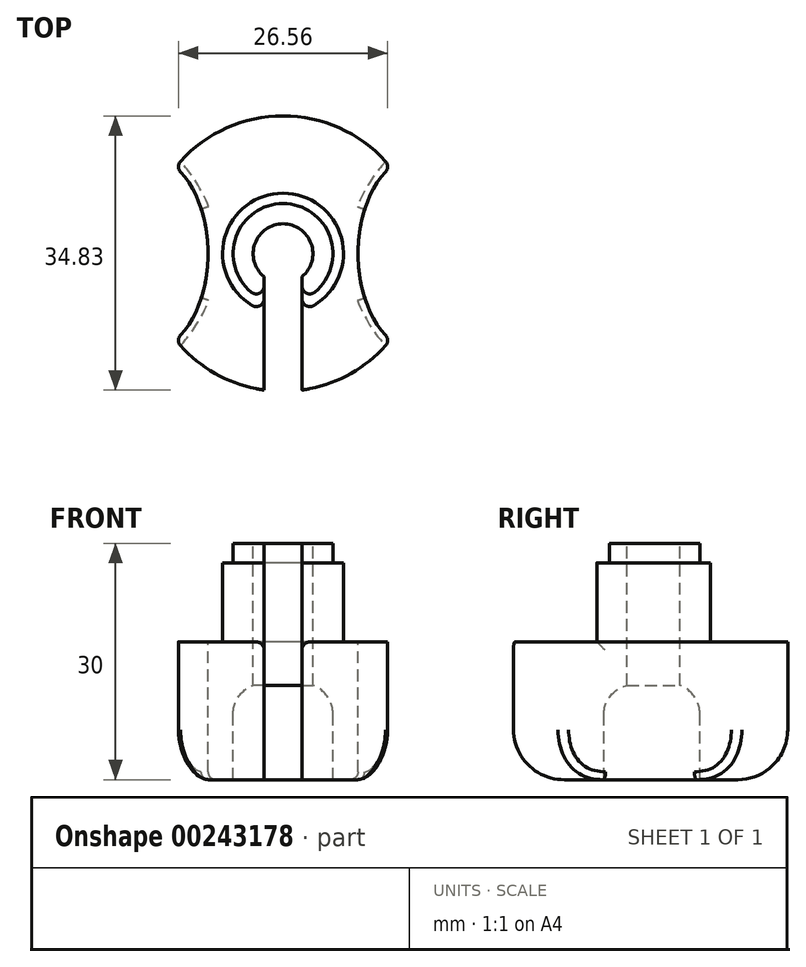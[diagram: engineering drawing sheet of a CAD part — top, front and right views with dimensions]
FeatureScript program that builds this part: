
annotation { "Feature Type Name" : "Feature", "Feature Type Description" : "" }
export const myFeature = defineFeature(function(context is Context, id is Id, definition is map)
    precondition{}
    {
        {
            var Q0;
            Q0=qCreatedBy(makeId("Top.planeOp"),FACE);
            var sketch = newSketch(context, id + "F0", { "sketchPlane" : qUnion([Q0])});
            skCircle(sketch, "E0", {"center": v(0, 0) * mm, "radius": 3.8 * mm});
            skCircle(sketch, "E1", {"center": v(0, 0) * mm, "radius": 6.35 * mm});
            skCircle(sketch, "E2", {"center": v(0, 0) * mm, "radius": 7.68 * mm});
            skCircle(sketch, "E3", {"center": v(0, 0) * mm, "radius": 17.5 * mm});
            skLineSegment(sketch, "E4", {"start": v(0, -2.92) * mm, "end": v(-2.41, -2.92) * mm});
            skLineSegment(sketch, "E5", {"start": v(0, -2.92) * mm, "end": v(2.41, -2.92) * mm});
            skLineSegment(sketch, "E6", {"start": v(-2.41, -2.92) * mm, "end": v(-2.41, -17.33) * mm});
            skLineSegment(sketch, "E7", {"start": v(2.41, -2.92) * mm, "end": v(2.41, -17.33) * mm});
            skLineSegment(sketch, "E8", {"start": v(0, 0) * mm, "end": v(-9.53, 0) * mm});
            skLineSegment(sketch, "E9", {"start": v(0, 0) * mm, "end": v(9.53, 0) * mm});
            skEllipse(sketch, "E10", {"center": v(17.5, 0) * mm, "majorRadius": 12.5 * mm, "minorRadius": 7.98 * mm, "majorAxis": v(0, 1)});
            skEllipse(sketch, "E11", {"center": v(-17.5, 0) * mm, "majorRadius": 12.5 * mm, "minorRadius": 7.98 * mm, "majorAxis": v(0, 1)});
            skSolve(sketch);
        }
        {
            var Q0;
            {var subQ0=sQuery(id+"F0.wireOp",EDGE,"E6");var subQ1=sQuery(id+"F0.wireOp",EDGE,"E2");var subQ2=makeQuery(id+"F0.imprint","INTERSECT",VERTEX,{"derivedFrom":[subQ1,subQ0]});Q0=makeQuery(id+"F0.imprint","IMPRINT",FACE,{"disambiguationData":[TD([[makeQuery(id+"F0.imprint","IMPRINT",EDGE,{"disambiguationData":[TD([[subQ2,1.0]])],"derivedFrom":subQ1}),-1.0]])]});}
            var Q1;
            {var subQ0=sQuery(id+"F0.wireOp",EDGE,"E6");var subQ1=sQuery(id+"F0.wireOp",EDGE,"E1");var subQ2=makeQuery(id+"F0.imprint","INTERSECT",VERTEX,{"derivedFrom":[subQ1,subQ0]});Q1=makeQuery(id+"F0.imprint","IMPRINT",FACE,{"disambiguationData":[TD([[makeQuery(id+"F0.imprint","IMPRINT",EDGE,{"disambiguationData":[TD([[subQ2,1.0]])],"derivedFrom":subQ1}),-1.0]])]});}
            var Q2;
            {var subQ0=sQuery(id+"F0.wireOp",EDGE,"E6");var subQ5=sQuery(id+"F0.wireOp",EDGE,"E1");var subQ6=makeQuery(id+"F0.imprint","INTERSECT",VERTEX,{"derivedFrom":[subQ5,subQ0]});Q2=makeQuery(id+"F0.imprint","IMPRINT",FACE,{"disambiguationData":[TD([[makeQuery(id+"F0.imprint","IMPRINT",EDGE,{"disambiguationData":[TD([[subQ6,1.0]])],"derivedFrom":subQ5}),1.0]])]});}
            var Q3;
            {var subQ0=sQuery(id+"F0.wireOp",EDGE,"PFdHEYGE-mdFE-cDqs-Gcgk-tPXnoa7n4Wt7");Q3=makeQuery(id+"F0.imprint","IMPRINT",FACE,{"disambiguationData":[TD([[makeQuery(id+"F0.imprint","IMPRINT",EDGE,{"derivedFrom":subQ0}),1.0]])]});}
            var Q4;
            {var subQ0=sQuery(id+"F0.wireOp",EDGE,"YKHqC44k-1NOB-Wwfc-Xhhn-dasVwciJDHPK");Q4=makeQuery(id+"F0.imprint","IMPRINT",FACE,{"disambiguationData":[TD([[makeQuery(id+"F0.imprint","IMPRINT",EDGE,{"derivedFrom":subQ0}),-1.0]])]});}
            var Q5;
            {var subQ3=sQuery(id+"F0.wireOp",EDGE,"E2");var subQ6=sQuery(id+"F0.wireOp",EDGE,"E8");var subQ8=makeQuery(id+"F0.imprint","INTERSECT",VERTEX,{"derivedFrom":[subQ3,subQ6]});Q5=makeQuery(id+"F0.imprint","IMPRINT",FACE,{"disambiguationData":[TD([[makeQuery(id+"F0.imprint","IMPRINT",EDGE,{"disambiguationData":[TD([[subQ8,1.0]])],"derivedFrom":subQ3}),-1.0]])]});}
            var Q6;
            {var subQ0=sQuery(id+"F0.wireOp",EDGE,"E8");var subQ1=sQuery(id+"F0.wireOp",EDGE,"E1");var subQ2=makeQuery(id+"F0.imprint","INTERSECT",VERTEX,{"derivedFrom":[subQ1,subQ0]});Q6=makeQuery(id+"F0.imprint","IMPRINT",FACE,{"disambiguationData":[TD([[makeQuery(id+"F0.imprint","IMPRINT",EDGE,{"disambiguationData":[TD([[subQ2,1.0]])],"derivedFrom":subQ1}),-1.0]])]});}
            var Q7;
            {var subQ0=sQuery(id+"F0.wireOp",EDGE,"E8");var subQ1=sQuery(id+"F0.wireOp",EDGE,"E0");var subQ2=makeQuery(id+"F0.imprint","INTERSECT",VERTEX,{"derivedFrom":[subQ1,subQ0]});Q7=makeQuery(id+"F0.imprint","IMPRINT",FACE,{"disambiguationData":[TD([[makeQuery(id+"F0.imprint","IMPRINT",EDGE,{"disambiguationData":[TD([[subQ2,1.0]])],"derivedFrom":subQ1}),-1.0]])]});}
            var Q8;
            {var subQ3=sQuery(id+"F0.wireOp",EDGE,"E9");var subQ5=sQuery(id+"F0.wireOp",EDGE,"E1");var subQ7=makeQuery(id+"F0.imprint","INTERSECT",VERTEX,{"derivedFrom":[subQ5,subQ3]});Q8=makeQuery(id+"F0.imprint","IMPRINT",FACE,{"disambiguationData":[TD([[makeQuery(id+"F0.imprint","IMPRINT",EDGE,{"disambiguationData":[TD([[subQ7,1.0]])],"derivedFrom":subQ5}),1.0]])]});}
            var Q9;
            {var subQ0=sQuery(id+"F0.wireOp",EDGE,"E9");var subQ1=sQuery(id+"F0.wireOp",EDGE,"E1");var subQ2=makeQuery(id+"F0.imprint","INTERSECT",VERTEX,{"derivedFrom":[subQ1,subQ0]});Q9=makeQuery(id+"F0.imprint","IMPRINT",FACE,{"disambiguationData":[TD([[makeQuery(id+"F0.imprint","IMPRINT",EDGE,{"disambiguationData":[TD([[subQ2,1.0]])],"derivedFrom":subQ1}),-1.0]])]});}
            var Q10;
            {var subQ1=sQuery(id+"F0.wireOp",EDGE,"E9");var subQ3=sQuery(id+"F0.wireOp",EDGE,"E2");var subQ4=makeQuery(id+"F0.imprint","INTERSECT",VERTEX,{"derivedFrom":[subQ3,subQ1]});Q10=makeQuery(id+"F0.imprint","IMPRINT",FACE,{"disambiguationData":[TD([[makeQuery(id+"F0.imprint","IMPRINT",EDGE,{"disambiguationData":[TD([[subQ4,1.0]])],"derivedFrom":subQ3}),-1.0]])]});}
            extrude(context, id + "F1", {"entities" : qUnion([Q0, Q1, Q2, Q3, Q4, Q5, Q6, Q7, Q8, Q9, Q10]), "oppositeDirection" : true, "depth" : 30 * mm});
        }
        {
            var Q0;
            {var subQ0=sQuery(id+"F0.wireOp",EDGE,"E6");var subQ1=sQuery(id+"F0.wireOp",EDGE,"E2");var subQ2=makeQuery(id+"F0.imprint","INTERSECT",VERTEX,{"derivedFrom":[subQ1,subQ0]});Q0=makeQuery(id+"F0.imprint","IMPRINT",FACE,{"disambiguationData":[TD([[makeQuery(id+"F0.imprint","IMPRINT",EDGE,{"disambiguationData":[TD([[subQ2,-1.0]])],"derivedFrom":subQ1}),-1.0]])]});}
            var Q1;
            {var subQ0=sQuery(id+"F0.wireOp",EDGE,"YKHqC44k-1NOB-Wwfc-Xhhn-dasVwciJDHPK");Q1=makeQuery(id+"F0.imprint","IMPRINT",FACE,{"disambiguationData":[TD([[makeQuery(id+"F0.imprint","IMPRINT",EDGE,{"derivedFrom":subQ0}),-1.0]])]});}
            var Q2;
            {var subQ0=sQuery(id+"F0.wireOp",EDGE,"PFdHEYGE-mdFE-cDqs-Gcgk-tPXnoa7n4Wt7");Q2=makeQuery(id+"F0.imprint","IMPRINT",FACE,{"disambiguationData":[TD([[makeQuery(id+"F0.imprint","IMPRINT",EDGE,{"derivedFrom":subQ0}),-1.0]])]});}
            var Q3;
            {var subQ0=sQuery(id+"F0.wireOp",EDGE,"PFdHEYGE-mdFE-cDqs-Gcgk-tPXnoa7n4Wt7");Q3=makeQuery(id+"F0.imprint","IMPRINT",FACE,{"disambiguationData":[TD([[makeQuery(id+"F0.imprint","IMPRINT",EDGE,{"derivedFrom":subQ0}),1.0]])]});}
            var Q4;
            {var subQ3=sQuery(id+"F0.wireOp",EDGE,"E2");var subQ6=sQuery(id+"F0.wireOp",EDGE,"E8");var subQ8=makeQuery(id+"F0.imprint","INTERSECT",VERTEX,{"derivedFrom":[subQ3,subQ6]});Q4=makeQuery(id+"F0.imprint","IMPRINT",FACE,{"disambiguationData":[TD([[makeQuery(id+"F0.imprint","IMPRINT",EDGE,{"disambiguationData":[TD([[subQ8,-1.0]])],"derivedFrom":subQ3}),-1.0]])]});}
            var Q5;
            {var subQ1=sQuery(id+"F0.wireOp",EDGE,"E9");var subQ3=sQuery(id+"F0.wireOp",EDGE,"E2");var subQ4=makeQuery(id+"F0.imprint","INTERSECT",VERTEX,{"derivedFrom":[subQ3,subQ1]});Q5=makeQuery(id+"F0.imprint","IMPRINT",FACE,{"disambiguationData":[TD([[makeQuery(id+"F0.imprint","IMPRINT",EDGE,{"disambiguationData":[TD([[subQ4,1.0]])],"derivedFrom":subQ3}),-1.0]])]});}
            var Q6;
            {var subQ3=sQuery(id+"F0.wireOp",EDGE,"E2");var subQ6=sQuery(id+"F0.wireOp",EDGE,"E8");var subQ8=makeQuery(id+"F0.imprint","INTERSECT",VERTEX,{"derivedFrom":[subQ3,subQ6]});Q6=makeQuery(id+"F0.imprint","IMPRINT",FACE,{"disambiguationData":[TD([[makeQuery(id+"F0.imprint","IMPRINT",EDGE,{"disambiguationData":[TD([[subQ8,1.0]])],"derivedFrom":subQ3}),-1.0]])]});}
            extrude(context, id + "F2", {"entities" : qUnion([Q0, Q1, Q2, Q3, Q4, Q5, Q6]), "operationType" : NewBodyOperationType.REMOVE, "oppositeDirection" : true, "depth" : 12.5 * mm});
        }
        {
            var Q0;
            {var subQ0=sQuery(id+"F0.wireOp",EDGE,"E6");var subQ1=sQuery(id+"F0.wireOp",EDGE,"E1");var subQ2=makeQuery(id+"F0.imprint","INTERSECT",VERTEX,{"derivedFrom":[subQ1,subQ0]});Q0=makeQuery(id+"F0.imprint","IMPRINT",FACE,{"disambiguationData":[TD([[makeQuery(id+"F0.imprint","IMPRINT",EDGE,{"disambiguationData":[TD([[subQ2,1.0]])],"derivedFrom":subQ1}),-1.0]])]});}
            var Q1;
            {var subQ0=sQuery(id+"F0.wireOp",EDGE,"E8");var subQ1=sQuery(id+"F0.wireOp",EDGE,"E1");var subQ2=makeQuery(id+"F0.imprint","INTERSECT",VERTEX,{"derivedFrom":[subQ1,subQ0]});Q1=makeQuery(id+"F0.imprint","IMPRINT",FACE,{"disambiguationData":[TD([[makeQuery(id+"F0.imprint","IMPRINT",EDGE,{"disambiguationData":[TD([[subQ2,1.0]])],"derivedFrom":subQ1}),-1.0]])]});}
            var Q2;
            {var subQ0=sQuery(id+"F0.wireOp",EDGE,"E9");var subQ1=sQuery(id+"F0.wireOp",EDGE,"E1");var subQ2=makeQuery(id+"F0.imprint","INTERSECT",VERTEX,{"derivedFrom":[subQ1,subQ0]});Q2=makeQuery(id+"F0.imprint","IMPRINT",FACE,{"disambiguationData":[TD([[makeQuery(id+"F0.imprint","IMPRINT",EDGE,{"disambiguationData":[TD([[subQ2,1.0]])],"derivedFrom":subQ1}),-1.0]])]});}
            extrude(context, id + "F3", {"entities" : qUnion([Q0, Q1, Q2]), "operationType" : NewBodyOperationType.REMOVE, "oppositeDirection" : true, "depth" : 2.45 * mm});
        }
        {
            var Q0;
            Q0=makeQuery(id+"F1.opExtrude","CAP_EDGE",EDGE,{"disambiguationData":[OSD([sQuery(id+"F0.wireOp",EDGE,"E3")])],"isStart":false});
            fillet(context, id + "F4", {"entities" : qUnion([Q0]), "radius" : 6.35 * mm, "tangentPropagation" : true, "allowEdgeOverflow" : false});
        }
        {
            var Q0;
            {var subQ0=sQuery(id+"F0.wireOp",EDGE,"E11");var subQ1=sQuery(id+"F0.wireOp",EDGE,"E3");Q0=makeQuery(id+"F1.opExtrude","SWEPT_EDGE",EDGE,{"disambiguationData":[OSD([subQ1,subQ0]),TDD([makeQuery(id+"F0.imprint","INTERSECT",VERTEX,{"disambiguationData":[OD(1.0)],"derivedFrom":[subQ1,subQ0]})])]});}
            fillet(context, id + "F5", {"entities" : qUnion([Q0]), "radius" : 1 * mm, "tangentPropagation" : true, "allowEdgeOverflow" : false});
        }
        {
            var Q0;
            {var subQ0=sQuery(id+"F0.wireOp",EDGE,"E10");var subQ1=sQuery(id+"F0.wireOp",EDGE,"E3");Q0=makeQuery(id+"F1.opExtrude","SWEPT_EDGE",EDGE,{"disambiguationData":[OSD([subQ1,subQ0]),TDD([makeQuery(id+"F0.imprint","INTERSECT",VERTEX,{"disambiguationData":[OD(0.0)],"derivedFrom":[subQ1,subQ0]})])]});}
            fillet(context, id + "F6", {"entities" : qUnion([Q0]), "radius" : 1 * mm, "tangentPropagation" : true, "allowEdgeOverflow" : false});
        }
        {
            var Q0;
            Q0=makeQuery(id+"F2.boolean.opBoolean","INTERSECT",EDGE,{"derivedFrom":[makeQuery(id+"F1.opExtrude","SWEPT_FACE",FACE,{"disambiguationData":[OSD([sQuery(id+"F0.wireOp",EDGE,"E6")])]}),makeQuery(id+"F2.opExtrude","CAP_FACE",FACE,{"disambiguationData":[OSD([sQuery(id+"F0.wireOp",EDGE,"E2"),sQuery(id+"F0.wireOp",EDGE,"E3"),sQuery(id+"F0.wireOp",EDGE,"E10"),sQuery(id+"F0.wireOp",EDGE,"E11")])],"isStart":false})]});
            var Q1;
            {var subQ0=sQuery(id+"F0.wireOp",EDGE,"E6");var subQ1=sQuery(id+"F0.wireOp",EDGE,"E3");var subQ2=makeQuery(id+"F0.imprint","INTERSECT",VERTEX,{"derivedFrom":[subQ1,subQ0]});var subQ4=makeQuery(id+"F0.imprint","IMPRINT",EDGE,{"disambiguationData":[TD([[subQ2,1.0]])],"derivedFrom":subQ1});var subQ6=makeQuery(id+"F0.imprint","INTERSECT",VERTEX,{"derivedFrom":[subQ1,sQuery(id+"F0.wireOp",EDGE,"E7")]});Q1=makeQuery(id+"F2.boolean.opBoolean","COPY",EDGE,{"disambiguationData":[TD([makeQuery(id+"F1.opExtrude","SWEPT_FACE",FACE,{"disambiguationData":[OSD([subQ0])]})])],"derivedFrom":makeQuery(id+"F2.opExtrude","CAP_EDGE",EDGE,{"disambiguationData":[OSD([subQ1]),TDD([subQ4,makeQuery(id+"F0.imprint","IMPRINT",EDGE,{"disambiguationData":[TD([[subQ2,-1.0]])],"derivedFrom":subQ1}),makeQuery(id+"F0.imprint","IMPRINT",EDGE,{"disambiguationData":[TD([[subQ6,-1.0]])],"derivedFrom":subQ1})])],"isStart":false})});}
            var Q2;
            Q2=makeQuery(id+"F2.boolean.opBoolean","COPY",EDGE,{"derivedFrom":makeQuery(id+"F2.opExtrude","CAP_EDGE",EDGE,{"disambiguationData":[OSD([sQuery(id+"F0.wireOp",EDGE,"E11")])],"isStart":false})});
            var Q3;
            Q3=makeQuery(id+"F2.boolean.opBoolean","INTERSECT",EDGE,{"derivedFrom":[makeQuery(id+"F1.opExtrude","SWEPT_FACE",FACE,{"disambiguationData":[OSD([sQuery(id+"F0.wireOp",EDGE,"E7")])]}),makeQuery(id+"F2.opExtrude","CAP_FACE",FACE,{"disambiguationData":[OSD([sQuery(id+"F0.wireOp",EDGE,"E2"),sQuery(id+"F0.wireOp",EDGE,"E3"),sQuery(id+"F0.wireOp",EDGE,"E10"),sQuery(id+"F0.wireOp",EDGE,"E11")])],"isStart":false})]});
            var Q4;
            Q4=makeQuery(id+"F2.boolean.opBoolean","INTERSECT",EDGE,{"derivedFrom":[makeQuery(id+"F1.opExtrude","SWEPT_FACE",FACE,{"disambiguationData":[OSD([sQuery(id+"F0.wireOp",EDGE,"E7")])]}),makeQuery(id+"F2.opExtrude","SWEPT_FACE",FACE,{"disambiguationData":[OSD([sQuery(id+"F0.wireOp",EDGE,"E2")])]})]});
            var Q5;
            Q5=makeQuery(id+"F2.boolean.opBoolean","INTERSECT",EDGE,{"derivedFrom":[makeQuery(id+"F1.opExtrude","SWEPT_FACE",FACE,{"disambiguationData":[OSD([sQuery(id+"F0.wireOp",EDGE,"E6")])]}),makeQuery(id+"F2.opExtrude","SWEPT_FACE",FACE,{"disambiguationData":[OSD([sQuery(id+"F0.wireOp",EDGE,"E2")])]})]});
            fillet(context, id + "F7", {"entities" : qUnion([Q0, Q1, Q2, Q3, Q4, Q5]), "radius" : 1 * mm, "tangentPropagation" : true, "allowEdgeOverflow" : false});
        }
        {
            var Q0;
            {var subQ3=sQuery(id+"F0.wireOp",EDGE,"E9");var subQ5=sQuery(id+"F0.wireOp",EDGE,"E1");var subQ7=makeQuery(id+"F0.imprint","INTERSECT",VERTEX,{"derivedFrom":[subQ5,subQ3]});Q0=makeQuery(id+"F0.imprint","IMPRINT",FACE,{"disambiguationData":[TD([[makeQuery(id+"F0.imprint","IMPRINT",EDGE,{"disambiguationData":[TD([[subQ7,1.0]])],"derivedFrom":subQ5}),1.0]])]});}
            var Q1;
            {var subQ0=sQuery(id+"F0.wireOp",EDGE,"E8");var subQ1=sQuery(id+"F0.wireOp",EDGE,"E0");var subQ2=makeQuery(id+"F0.imprint","INTERSECT",VERTEX,{"derivedFrom":[subQ1,subQ0]});Q1=makeQuery(id+"F0.imprint","IMPRINT",FACE,{"disambiguationData":[TD([[makeQuery(id+"F0.imprint","IMPRINT",EDGE,{"disambiguationData":[TD([[subQ2,1.0]])],"derivedFrom":subQ1}),-1.0]])]});}
            var Q2;
            {var subQ3=sQuery(id+"F0.wireOp",EDGE,"E8");var subQ5=sQuery(id+"F0.wireOp",EDGE,"E1");var subQ6=makeQuery(id+"F0.imprint","INTERSECT",VERTEX,{"derivedFrom":[subQ5,subQ3]});Q2=makeQuery(id+"F0.imprint","IMPRINT",FACE,{"disambiguationData":[TD([[makeQuery(id+"F0.imprint","IMPRINT",EDGE,{"disambiguationData":[TD([[subQ6,-1.0]])],"derivedFrom":subQ5}),1.0]])]});}
            extrude(context, id + "F8", {"entities" : qUnion([Q0, Q1, Q2]), "operationType" : NewBodyOperationType.REMOVE, "oppositeDirection" : true, "depth" : 35 * mm, "hasSecondDirection" : true, "secondDirectionOppositeDirection" : true, "secondDirectionDepth" : 18 * mm});
        }
        {
            var Q0;
            Q0=makeQuery(id+"F8.boolean.opBoolean","COPY",EDGE,{"derivedFrom":makeQuery(id+"F8.opExtrude","CAP_EDGE",EDGE,{"disambiguationData":[OSD([sQuery(id+"F0.wireOp",EDGE,"E1")])],"isStart":true})});
            fillet(context, id + "F9", {"entities" : qUnion([Q0]), "radius" : 4 * mm, "tangentPropagation" : true, "allowEdgeOverflow" : false});
        }
        {
            var Q0;
            Q0=makeQuery(id+"F7.opFillet","BLEND_EDGE",EDGE,{"blendedFrom":[makeQuery(id+"F2.boolean.opBoolean","INTERSECT",EDGE,{"derivedFrom":[makeQuery(id+"F1.opExtrude","SWEPT_FACE",FACE,{"disambiguationData":[OSD([sQuery(id+"F0.wireOp",EDGE,"E6")])]}),makeQuery(id+"F2.opExtrude","SWEPT_FACE",FACE,{"disambiguationData":[OSD([sQuery(id+"F0.wireOp",EDGE,"E2")])]})]}),makeQuery(id+"F3.boolean.opBoolean","COPY",FACE,{"derivedFrom":makeQuery(id+"F3.opExtrude","SWEPT_FACE",FACE,{"disambiguationData":[OSD([sQuery(id+"F0.wireOp",EDGE,"E1")])]})})],"blendedInto":[makeQuery(id+"F3.boolean.opBoolean","COPY",FACE,{"derivedFrom":makeQuery(id+"F3.opExtrude","SWEPT_FACE",FACE,{"disambiguationData":[OSD([sQuery(id+"F0.wireOp",EDGE,"E1")])]})})]});
            var Q1;
            Q1=makeQuery(id+"F7.opFillet","BLEND_EDGE",EDGE,{"blendedFrom":[makeQuery(id+"F2.boolean.opBoolean","INTERSECT",EDGE,{"derivedFrom":[makeQuery(id+"F1.opExtrude","SWEPT_FACE",FACE,{"disambiguationData":[OSD([sQuery(id+"F0.wireOp",EDGE,"E7")])]}),makeQuery(id+"F2.opExtrude","SWEPT_FACE",FACE,{"disambiguationData":[OSD([sQuery(id+"F0.wireOp",EDGE,"E2")])]})]}),makeQuery(id+"F3.boolean.opBoolean","COPY",FACE,{"derivedFrom":makeQuery(id+"F3.opExtrude","SWEPT_FACE",FACE,{"disambiguationData":[OSD([sQuery(id+"F0.wireOp",EDGE,"E1")])]})})],"blendedInto":[makeQuery(id+"F3.boolean.opBoolean","COPY",FACE,{"derivedFrom":makeQuery(id+"F3.opExtrude","SWEPT_FACE",FACE,{"disambiguationData":[OSD([sQuery(id+"F0.wireOp",EDGE,"E1")])]})})]});
            fillet(context, id + "F10", {"entities" : qUnion([Q0, Q1]), "radius" : 1 * mm, "tangentPropagation" : true, "allowEdgeOverflow" : false});
        }
    });
